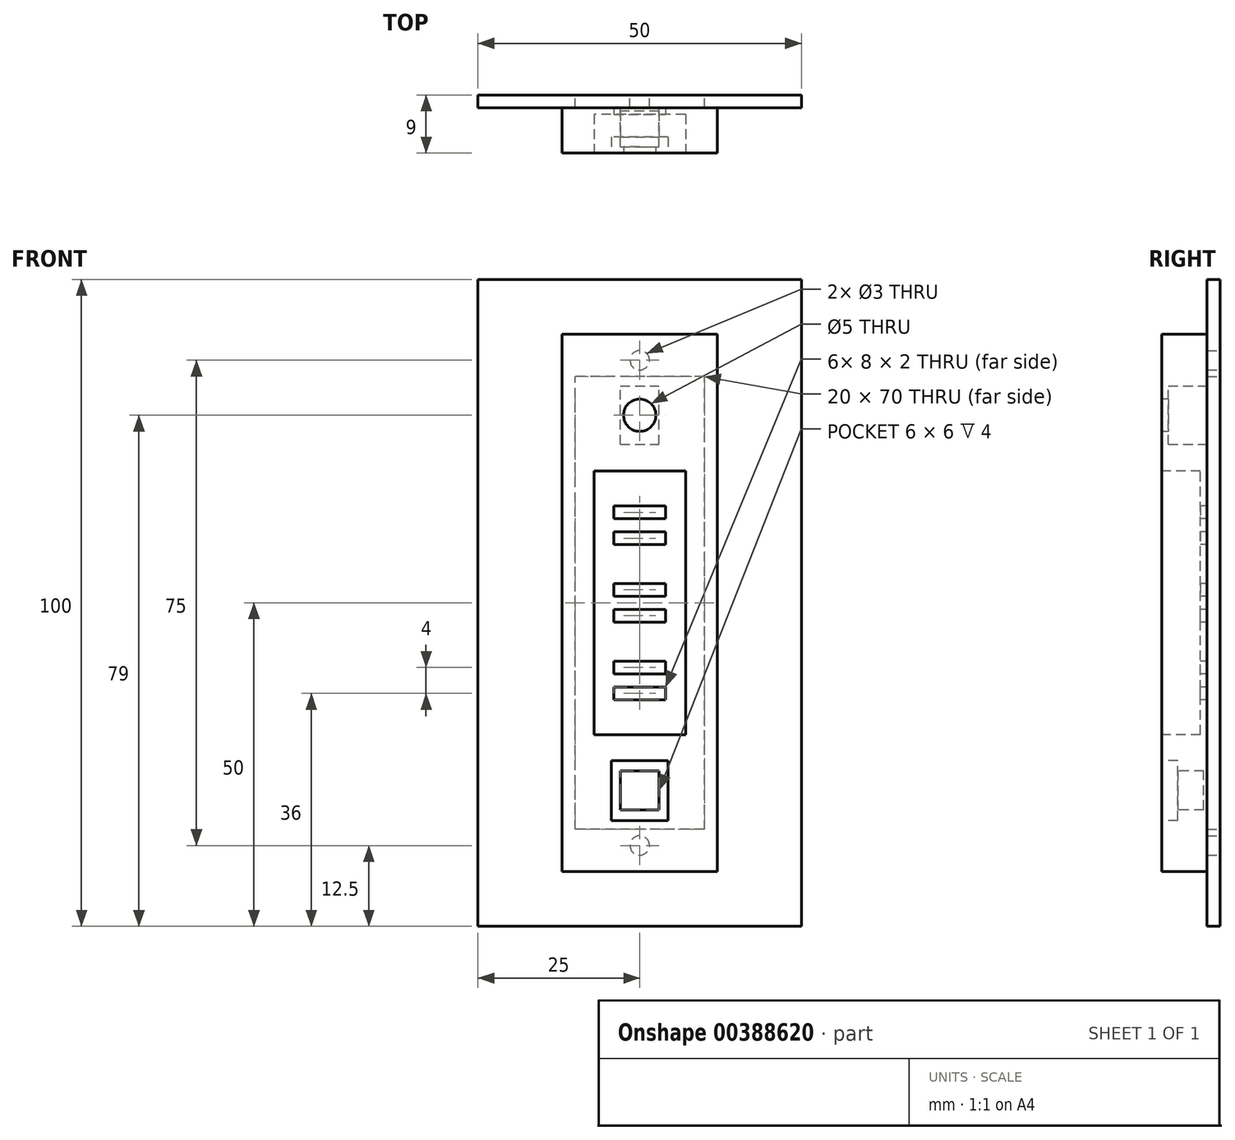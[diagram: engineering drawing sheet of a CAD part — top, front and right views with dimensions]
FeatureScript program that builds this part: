
annotation { "Feature Type Name" : "Feature", "Feature Type Description" : "" }
export const myFeature = defineFeature(function(context is Context, id is Id, definition is map)
    precondition{}
    {
        {
            var Q0;
            Q0=qCreatedBy(makeId("Front.planeOp"),FACE);
            var sketch = newSketch(context, id + "F0", { "sketchPlane" : qUnion([Q0])});
            skLineSegment(sketch, "E0.bottom", {"start": v(25, -50) * mm, "end": v(-25, -50) * mm});
            skLineSegment(sketch, "E0.top", {"start": v(25, 50) * mm, "end": v(-25, 50) * mm});
            skLineSegment(sketch, "E0.left", {"start": v(25, -50) * mm, "end": v(25, 50) * mm});
            skLineSegment(sketch, "E0.right", {"start": v(-25, -50) * mm, "end": v(-25, 50) * mm});
            skPoint(sketch, "E0.middle", {"position": v(0, 0) * mm});
            skLineSegment(sketch, "E1.bottom", {"start": v(10, -35) * mm, "end": v(-10, -35) * mm});
            skLineSegment(sketch, "E1.top", {"start": v(10, 35) * mm, "end": v(-10, 35) * mm});
            skLineSegment(sketch, "E1.left", {"start": v(10, -35) * mm, "end": v(10, 35) * mm});
            skLineSegment(sketch, "E1.right", {"start": v(-10, -35) * mm, "end": v(-10, 35) * mm});
            skCircle(sketch, "E2", {"center": v(0, 37.5) * mm, "radius": 1.5 * mm});
            skCircle(sketch, "E3", {"center": v(0, -37.5) * mm, "radius": 1.5 * mm});
            skSolve(sketch);
        }
        {
            var Q0;
            Q0=qSketchRegion(id+"F0",true);
            extrude(context, id + "F1", {"entities" : qUnion([Q0]), "depth" : 2 * mm});
        }
        {
            var Q0;
            Q0=makeQuery(id+"F1.opExtrude","CAP_FACE",FACE,{"disambiguationData":[OSD([sQuery(id+"F0.wireOp",EDGE,"E0.bottom"),sQuery(id+"F0.wireOp",EDGE,"E0.top"),sQuery(id+"F0.wireOp",EDGE,"E0.left"),sQuery(id+"F0.wireOp",EDGE,"E0.right"),sQuery(id+"F0.wireOp",EDGE,"E1.bottom"),sQuery(id+"F0.wireOp",EDGE,"E1.top"),sQuery(id+"F0.wireOp",EDGE,"E1.left"),sQuery(id+"F0.wireOp",EDGE,"E1.right"),sQuery(id+"F0.wireOp",EDGE,"E2"),sQuery(id+"F0.wireOp",EDGE,"E3")])],"isStart":false});
            cPlane(context, id + "F2", {"entities" : qUnion([Q0]), "cplaneType" : CPlaneType.OFFSET, "offset" : 0 * mm, "width" : 150 * mm, "height" : 150 * mm});
        }
        {
            var Q0;
            Q0=qCreatedBy(id+"F2.planeOp",FACE);
            var sketch = newSketch(context, id + "F3", { "sketchPlane" : qUnion([Q0])});
            skLineSegment(sketch, "E4.bottom", {"start": v(12, -41.5) * mm, "end": v(-12, -41.5) * mm});
            skLineSegment(sketch, "E4.top", {"start": v(12, 41.5) * mm, "end": v(-12, 41.5) * mm});
            skLineSegment(sketch, "E4.left", {"start": v(12, -41.5) * mm, "end": v(12, 41.5) * mm});
            skLineSegment(sketch, "E4.right", {"start": v(-12, -41.5) * mm, "end": v(-12, 41.5) * mm});
            skPoint(sketch, "E4.middle", {"position": v(0, 0) * mm});
            skSolve(sketch);
        }
        {
            var Q0;
            Q0=qSketchRegion(id+"F3",true);
            extrude(context, id + "F4", {"entities" : qUnion([Q0]), "depth" : 7 * mm});
        }
        {
            var Q0;
            Q0=makeQuery(id+"F4.opExtrude","CAP_FACE",FACE,{"disambiguationData":[OSD([sQuery(id+"F3.wireOp",EDGE,"E4.bottom"),sQuery(id+"F3.wireOp",EDGE,"E4.top"),sQuery(id+"F3.wireOp",EDGE,"E4.left"),sQuery(id+"F3.wireOp",EDGE,"E4.right")])],"isStart":false});
            var sketch = newSketch(context, id + "F5", { "sketchPlane" : qUnion([Q0])});
            skCircle(sketch, "E5", {"center": v(0, 29) * mm, "radius": 2.5 * mm});
            skLineSegment(sketch, "E6.bottom", {"start": v(2.5, 25) * mm, "end": v(-2.5, 25) * mm, "construction": true});
            skLineSegment(sketch, "E6.top", {"start": v(2.5, 33) * mm, "end": v(-2.5, 33) * mm, "construction": true});
            skLineSegment(sketch, "E6.left", {"start": v(2.5, 25) * mm, "end": v(2.5, 33) * mm, "construction": true});
            skLineSegment(sketch, "E6.right", {"start": v(-2.5, 25) * mm, "end": v(-2.5, 33) * mm, "construction": true});
            skCircle(sketch, "E7", {"center": v(-7.5, 32.5) * mm, "radius": 1 * mm, "construction": true});
            skCircle(sketch, "E8", {"center": v(7.5, 32.5) * mm, "radius": 1 * mm, "construction": true});
            skCircle(sketch, "E9", {"center": v(-7.5, -32.5) * mm, "radius": 1 * mm, "construction": true});
            skCircle(sketch, "E10", {"center": v(7.5, -32.5) * mm, "radius": 1 * mm, "construction": true});
            skSolve(sketch);
        }
        {
            var Q0;
            Q0=qSketchRegion(id+"F5",true);
            extrude(context, id + "F6", {"entities" : qUnion([Q0]), "operationType" : NewBodyOperationType.REMOVE, "oppositeDirection" : true, "depth" : 5 * mm});
        }
        {
            var Q0;
            Q0=makeQuery(id+"F4.opExtrude","CAP_FACE",FACE,{"disambiguationData":[OSD([sQuery(id+"F3.wireOp",EDGE,"E4.bottom"),sQuery(id+"F3.wireOp",EDGE,"E4.top"),sQuery(id+"F3.wireOp",EDGE,"E4.left"),sQuery(id+"F3.wireOp",EDGE,"E4.right")])],"isStart":true});
            var sketch = newSketch(context, id + "F7", { "sketchPlane" : qUnion([Q0])});
            skLineSegment(sketch, "E11.bottom", {"start": v(3, 24.5) * mm, "end": v(-3, 24.5) * mm});
            skLineSegment(sketch, "E11.top", {"start": v(3, 33.5) * mm, "end": v(-3, 33.5) * mm});
            skLineSegment(sketch, "E11.left", {"start": v(3, 24.5) * mm, "end": v(3, 33.5) * mm});
            skLineSegment(sketch, "E11.right", {"start": v(-3, 24.5) * mm, "end": v(-3, 33.5) * mm});
            skPoint(sketch, "E11.middle", {"position": v(0, 29) * mm});
            skSolve(sketch);
        }
        {
            var Q0;
            Q0=qSketchRegion(id+"F7",true);
            extrude(context, id + "F8", {"entities" : qUnion([Q0]), "operationType" : NewBodyOperationType.REMOVE, "oppositeDirection" : true, "depth" : 6 * mm});
        }
        {
            var Q0;
            Q0=makeQuery(id+"F4.opExtrude","CAP_FACE",FACE,{"disambiguationData":[OSD([sQuery(id+"F3.wireOp",EDGE,"E4.bottom"),sQuery(id+"F3.wireOp",EDGE,"E4.top"),sQuery(id+"F3.wireOp",EDGE,"E4.left"),sQuery(id+"F3.wireOp",EDGE,"E4.right")])],"isStart":false});
            var sketch = newSketch(context, id + "F9", { "sketchPlane" : qUnion([Q0])});
            skLineSegment(sketch, "E12.bottom", {"start": v(4, 13) * mm, "end": v(-4, 13) * mm});
            skLineSegment(sketch, "E12.top", {"start": v(4, 15) * mm, "end": v(-4, 15) * mm});
            skLineSegment(sketch, "E12.left", {"start": v(4, 13) * mm, "end": v(4, 15) * mm});
            skLineSegment(sketch, "E12.right", {"start": v(-4, 13) * mm, "end": v(-4, 15) * mm});
            skPoint(sketch, "E12.middle", {"position": v(0, 14) * mm});
            skLineSegment(sketch, "E13.bottom", {"start": v(4, 9) * mm, "end": v(-4, 9) * mm});
            skLineSegment(sketch, "E13.top", {"start": v(4, 11) * mm, "end": v(-4, 11) * mm});
            skLineSegment(sketch, "E13.left", {"start": v(4, 9) * mm, "end": v(4, 11) * mm});
            skLineSegment(sketch, "E13.right", {"start": v(-4, 9) * mm, "end": v(-4, 11) * mm});
            skPoint(sketch, "E13.middle", {"position": v(0, 10) * mm});
            skLineSegment(sketch, "E14.bottom", {"start": v(4, 1) * mm, "end": v(-4, 1) * mm});
            skLineSegment(sketch, "E14.top", {"start": v(4, 3) * mm, "end": v(-4, 3) * mm});
            skLineSegment(sketch, "E14.left", {"start": v(4, 1) * mm, "end": v(4, 3) * mm});
            skLineSegment(sketch, "E14.right", {"start": v(-4, 1) * mm, "end": v(-4, 3) * mm});
            skPoint(sketch, "E14.middle", {"position": v(0, 2) * mm});
            skLineSegment(sketch, "E15.bottom", {"start": v(4, -1) * mm, "end": v(-4, -1) * mm});
            skLineSegment(sketch, "E15.top", {"start": v(4, -3) * mm, "end": v(-4, -3) * mm});
            skLineSegment(sketch, "E15.left", {"start": v(4, -1) * mm, "end": v(4, -3) * mm});
            skLineSegment(sketch, "E15.right", {"start": v(-4, -1) * mm, "end": v(-4, -3) * mm});
            skPoint(sketch, "E15.middle", {"position": v(0, -2) * mm});
            skLineSegment(sketch, "E16.bottom", {"start": v(4, -9) * mm, "end": v(-4, -9) * mm});
            skLineSegment(sketch, "E16.top", {"start": v(4, -11) * mm, "end": v(-4, -11) * mm});
            skLineSegment(sketch, "E16.left", {"start": v(4, -9) * mm, "end": v(4, -11) * mm});
            skLineSegment(sketch, "E16.right", {"start": v(-4, -9) * mm, "end": v(-4, -11) * mm});
            skPoint(sketch, "E16.middle", {"position": v(0, -10) * mm});
            skPoint(sketch, "E16.middle.positionSnap0", {"position": v(0, -3) * mm});
            skPoint(sketch, "E16.centerSnap0", {"position": v(0, -3) * mm});
            skLineSegment(sketch, "E17.bottom", {"start": v(4, -13) * mm, "end": v(-4, -13) * mm});
            skLineSegment(sketch, "E17.top", {"start": v(4, -15) * mm, "end": v(-4, -15) * mm});
            skLineSegment(sketch, "E17.left", {"start": v(4, -13) * mm, "end": v(4, -15) * mm});
            skLineSegment(sketch, "E17.right", {"start": v(-4, -13) * mm, "end": v(-4, -15) * mm});
            skPoint(sketch, "E17.middle", {"position": v(0, -14) * mm});
            skSolve(sketch);
        }
        {
            var Q0;
            Q0=qSketchRegion(id+"F9",true);
            extrude(context, id + "F10", {"entities" : qUnion([Q0]), "operationType" : NewBodyOperationType.REMOVE, "oppositeDirection" : true, "depth" : 10 * mm});
        }
        {
            var Q0;
            Q0=makeQuery(id+"F4.opExtrude","CAP_FACE",FACE,{"disambiguationData":[OSD([sQuery(id+"F3.wireOp",EDGE,"E4.bottom"),sQuery(id+"F3.wireOp",EDGE,"E4.top"),sQuery(id+"F3.wireOp",EDGE,"E4.left"),sQuery(id+"F3.wireOp",EDGE,"E4.right")])],"isStart":false});
            var sketch = newSketch(context, id + "F11", { "sketchPlane" : qUnion([Q0])});
            skLineSegment(sketch, "E18.bottom", {"start": v(7.07, -20.36) * mm, "end": v(-7.07, -20.36) * mm});
            skLineSegment(sketch, "E18.top", {"start": v(7.07, 20.36) * mm, "end": v(-7.07, 20.36) * mm});
            skLineSegment(sketch, "E18.left", {"start": v(7.07, -20.36) * mm, "end": v(7.07, 20.36) * mm});
            skLineSegment(sketch, "E18.right", {"start": v(-7.07, -20.36) * mm, "end": v(-7.07, 20.36) * mm});
            skPoint(sketch, "E18.middle", {"position": v(0, 0) * mm});
            skSolve(sketch);
        }
        {
            var Q0;
            Q0=qSketchRegion(id+"F11",true);
            extrude(context, id + "F12", {"entities" : qUnion([Q0]), "operationType" : NewBodyOperationType.REMOVE, "oppositeDirection" : true, "depth" : 6 * mm});
        }
        {
            var Q0;
            Q0=makeQuery(id+"F4.opExtrude","CAP_FACE",FACE,{"disambiguationData":[OSD([sQuery(id+"F3.wireOp",EDGE,"E4.bottom"),sQuery(id+"F3.wireOp",EDGE,"E4.top"),sQuery(id+"F3.wireOp",EDGE,"E4.left"),sQuery(id+"F3.wireOp",EDGE,"E4.right")])],"isStart":false});
            var sketch = newSketch(context, id + "F13", { "sketchPlane" : qUnion([Q0])});
            skLineSegment(sketch, "E19.bottom", {"start": v(3, -32) * mm, "end": v(-3, -32) * mm});
            skLineSegment(sketch, "E19.top", {"start": v(3, -26) * mm, "end": v(-3, -26) * mm});
            skLineSegment(sketch, "E19.left", {"start": v(3, -32) * mm, "end": v(3, -26) * mm});
            skLineSegment(sketch, "E19.right", {"start": v(-3, -32) * mm, "end": v(-3, -26) * mm});
            skPoint(sketch, "E19.middle", {"position": v(0, -29) * mm});
            skSolve(sketch);
        }
        {
            var Q0;
            Q0=qSketchRegion(id+"F13",true);
            extrude(context, id + "F14", {"entities" : qUnion([Q0]), "operationType" : NewBodyOperationType.REMOVE, "oppositeDirection" : true, "depth" : 6.5 * mm});
        }
        {
            var Q0;
            Q0=makeQuery(id+"F4.opExtrude","CAP_FACE",FACE,{"disambiguationData":[OSD([sQuery(id+"F3.wireOp",EDGE,"E4.bottom"),sQuery(id+"F3.wireOp",EDGE,"E4.top"),sQuery(id+"F3.wireOp",EDGE,"E4.left"),sQuery(id+"F3.wireOp",EDGE,"E4.right")])],"isStart":false});
            var sketch = newSketch(context, id + "F15", { "sketchPlane" : qUnion([Q0])});
            skLineSegment(sketch, "E20.bottom", {"start": v(4.4, -33.62) * mm, "end": v(-4.4, -33.62) * mm});
            skLineSegment(sketch, "E20.top", {"start": v(4.4, -24.38) * mm, "end": v(-4.4, -24.38) * mm});
            skLineSegment(sketch, "E20.left", {"start": v(4.4, -33.62) * mm, "end": v(4.4, -24.38) * mm});
            skLineSegment(sketch, "E20.right", {"start": v(-4.4, -33.62) * mm, "end": v(-4.4, -24.38) * mm});
            skPoint(sketch, "E20.middle", {"position": v(0, -29) * mm});
            skPoint(sketch, "E20.middle.positionSnap0", {"position": v(0, -26) * mm});
            skPoint(sketch, "E20.middle.positionSnap1", {"position": v(3, -29) * mm});
            skPoint(sketch, "E20.centerSnap0", {"position": v(0, -26) * mm});
            skPoint(sketch, "E20.centerSnap1", {"position": v(3, -29) * mm});
            skSolve(sketch);
        }
        {
            var Q0;
            Q0 = qSketchRegion(id + "F15", true);
            extrude(context, id + "F16", {"entities" : qUnion([Q0]), "operationType" : NewBodyOperationType.REMOVE, "oppositeDirection" : true, "depth" : 2.5 * mm});
        }
    });
